# Revit family: Resan Shelf
name_source: partatom
category: Furniture
revit_build: Autodesk Revit MEP 2014 (Build: 20130308_1515(x64)
units: mm (PartAtom-declared; Revit-internal decimal feet)

## types (2) — shared parameters
Anti-Vandal = Yes
Colour = White
Coverage Area = 0.01m^3
Default Elevation = 1219 mm
Description = Shelf
EAN Number = 5013241059176
Features = Anti-Vandal
Gross Weight = 7.6KG
Installation Type = Wall
Issue = 1
Manufacturer = Thomas Dudley Ltd
Manufacturer Country = United Kingdom
Material = Polyester Resin
Model = Resan Anto-Ligature Shelf
Optional Peripherals = Resan Mirror
Overall Height = 195 mm  [stored 0.639764 ft]
Overall Length = 106 mm
Overall Width = 520 mm  [stored 1.70604 ft]
Product Instructions = http://www.thomasdudley.co.uk
Product Literature = http://www.dudleyresan.co.uk
Product Range = Resan
Publish Date = 11/02/2016
Servicing = Refer to instructions
Shape = Triangular
Shipping Weight = 8.5KG
Spares = http://spares.thomasdudley.co.uk
Type = Shelf
URL = www.thomasdudley.co.uk
Warranty = Parts
Warranty Type = 5 Years
YouTube Link = https://youtu.be
zero-valued in all types: Access Clearance Bottom, Access Clearance Front, Access Clearance Left, Access Clearance Rear, Access Clearance Right, Access Clearance Top

## per-type parameters (varying)
| type | Material Finishes | Product Code |
| 326145 Resan Shelf - Matt Finish | Stonecast Matt White | PRESSH326145 |
| 326144 Resan Shelf - Polished Gloss Finish | Polished Gloss White | PRESSH326144 |

note: [stored X ft] marks values corroborated as IEEE doubles in the binary element streams (Revit-internal decimal feet)

## geometry (parser evidence)
native form markers: Sweep x1
no freeform markers — native parametric forms only
